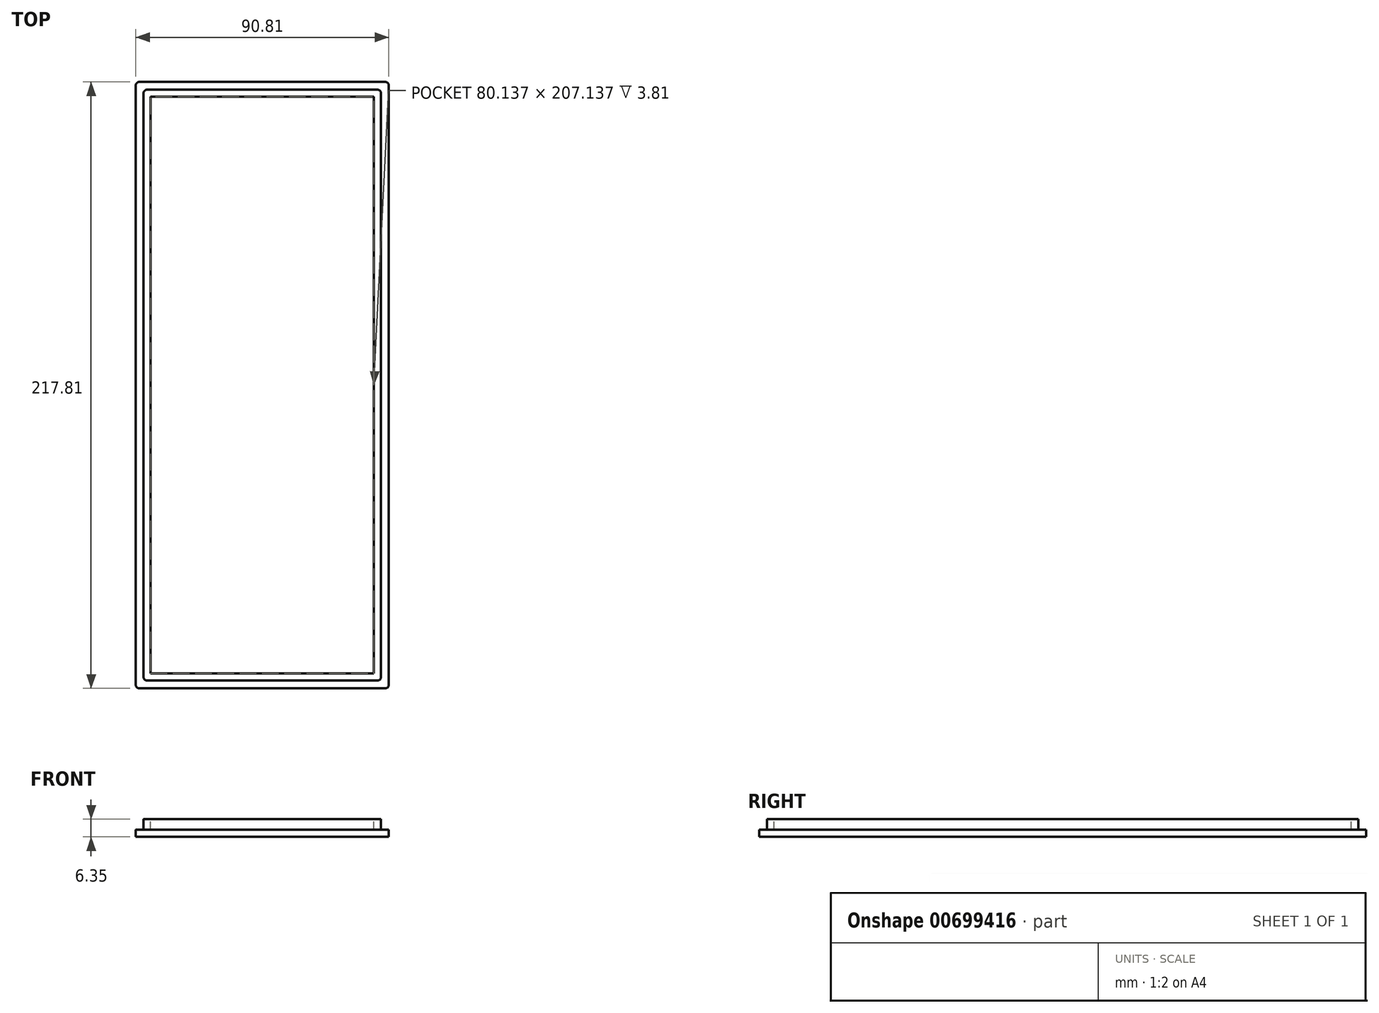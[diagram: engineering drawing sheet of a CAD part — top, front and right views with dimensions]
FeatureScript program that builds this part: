
annotation { "Feature Type Name" : "Feature", "Feature Type Description" : "" }
export const myFeature = defineFeature(function(context is Context, id is Id, definition is map)
    precondition{}
    {
        {
            var Q0;
            Q0=qCreatedBy(makeId("Top.planeOp"),FACE);
            var sketch = newSketch(context, id + "F0", { "sketchPlane" : qUnion([Q0])});
            skLineSegment(sketch, "E0.bottom", {"start": v(1.27, 0) * mm, "end": v(89.53, 0) * mm});
            skLineSegment(sketch, "E0.top", {"start": v(1.27, 217.8) * mm, "end": v(89.53, 217.8) * mm});
            skLineSegment(sketch, "E0.left", {"start": v(0, 1.27) * mm, "end": v(0, 216.53) * mm});
            skLineSegment(sketch, "E0.right", {"start": v(90.8, 1.27) * mm, "end": v(90.8, 216.53) * mm});
            skPoint(sketch, "E1.visualSharp", {"position": v(0, 217.8) * mm});
            skArc(sketch, "E1.filletArc", {"start": v(1.27, 217.8) * mm, "mid": v(0.37, 217.43) * mm, "end": v(0, 216.53) * mm});
            skPoint(sketch, "E2.visualSharp", {"position": v(90.8, 217.8) * mm});
            skArc(sketch, "E2.filletArc", {"start": v(90.8, 216.53) * mm, "mid": v(90.43, 217.43) * mm, "end": v(89.53, 217.8) * mm});
            skPoint(sketch, "E3.visualSharp", {"position": v(90.8, 0) * mm});
            skArc(sketch, "E3.filletArc", {"start": v(89.53, 0) * mm, "mid": v(90.43, 0.37) * mm, "end": v(90.8, 1.27) * mm});
            skPoint(sketch, "E4.visualSharp", {"position": v(0, 0) * mm});
            skArc(sketch, "E4.filletArc", {"start": v(0, 1.27) * mm, "mid": v(0.37, 0.37) * mm, "end": v(1.27, 0) * mm});
            skSolve(sketch);
        }
        {
            var Q0;
            Q0=qSketchRegion(id+"F0",true);
            extrude(context, id + "F1", {"entities" : qUnion([Q0]), "depth" : 2.54 * mm, "offsetDistance" : 25.4 * mm});
        }
        {
            var Q0;
            Q0=qCreatedBy(makeId("Top.planeOp"),FACE);
            var sketch = newSketch(context, id + "F2", { "sketchPlane" : qUnion([Q0])});
            skLineSegment(sketch, "E5.0", {"start": v(2.8, 4.06) * mm, "end": v(2.8, 213.74) * mm});
            skLineSegment(sketch, "E5.1", {"start": v(4.06, 2.8) * mm, "end": v(86.74, 2.8) * mm});
            skLineSegment(sketch, "E5.2", {"start": v(88.01, 4.06) * mm, "end": v(88.01, 213.74) * mm});
            skLineSegment(sketch, "E5.3", {"start": v(4.06, 215.01) * mm, "end": v(86.74, 215.01) * mm});
            skPoint(sketch, "E6.visualSharp", {"position": v(2.8, 215.01) * mm});
            skArc(sketch, "E6.filletArc", {"start": v(4.06, 215.01) * mm, "mid": v(3.17, 214.64) * mm, "end": v(2.8, 213.74) * mm});
            skPoint(sketch, "E7.visualSharp", {"position": v(88.01, 215.01) * mm});
            skArc(sketch, "E7.filletArc", {"start": v(88.01, 213.74) * mm, "mid": v(87.64, 214.64) * mm, "end": v(86.74, 215.01) * mm});
            skPoint(sketch, "E8.visualSharp", {"position": v(88.01, 2.8) * mm});
            skArc(sketch, "E8.filletArc", {"start": v(86.74, 2.8) * mm, "mid": v(87.64, 3.17) * mm, "end": v(88.01, 4.06) * mm});
            skPoint(sketch, "E9.visualSharp", {"position": v(2.8, 2.8) * mm});
            skArc(sketch, "E9.filletArc", {"start": v(2.8, 4.06) * mm, "mid": v(3.17, 3.17) * mm, "end": v(4.06, 2.8) * mm});
            skSolve(sketch);
        }
        {
            var Q0;
            Q0=qSketchRegion(id+"F2",true);
            extrude(context, id + "F3", {"entities" : qUnion([Q0]), "operationType" : NewBodyOperationType.ADD, "depth" : 6.35 * mm, "offsetDistance" : 25.4 * mm});
        }
        {
            var Q0;
            Q0=makeQuery(id+"F3.opExtrude","CAP_FACE",FACE,{"disambiguationData":[OSD([sQuery(id+"F2.wireOp",EDGE,"E5.0"),sQuery(id+"F2.wireOp",EDGE,"E5.1"),sQuery(id+"F2.wireOp",EDGE,"E5.2"),sQuery(id+"F2.wireOp",EDGE,"E5.3"),sQuery(id+"F2.wireOp",EDGE,"E6.filletArc"),sQuery(id+"F2.wireOp",EDGE,"E7.filletArc"),sQuery(id+"F2.wireOp",EDGE,"E8.filletArc"),sQuery(id+"F2.wireOp",EDGE,"E9.filletArc")])],"isStart":false});
            var sketch = newSketch(context, id + "F4", { "sketchPlane" : qUnion([Q0])});
            skLineSegment(sketch, "E10.0", {"start": v(5.33, 5.33) * mm, "end": v(5.33, 212.47) * mm});
            skLineSegment(sketch, "E10.1", {"start": v(5.33, 5.33) * mm, "end": v(85.47, 5.33) * mm});
            skLineSegment(sketch, "E10.2", {"start": v(85.47, 5.33) * mm, "end": v(85.47, 212.47) * mm});
            skLineSegment(sketch, "E10.3", {"start": v(5.33, 212.47) * mm, "end": v(85.47, 212.47) * mm});
            skSolve(sketch);
        }
        {
            var Q0;
            Q0=qSketchRegion(id+"F4",true);
            extrude(context, id + "F5", {"entities" : qUnion([Q0]), "operationType" : NewBodyOperationType.REMOVE, "oppositeDirection" : true, "depth" : 3.8 * mm, "offsetDistance" : 25.4 * mm});
        }
    });
